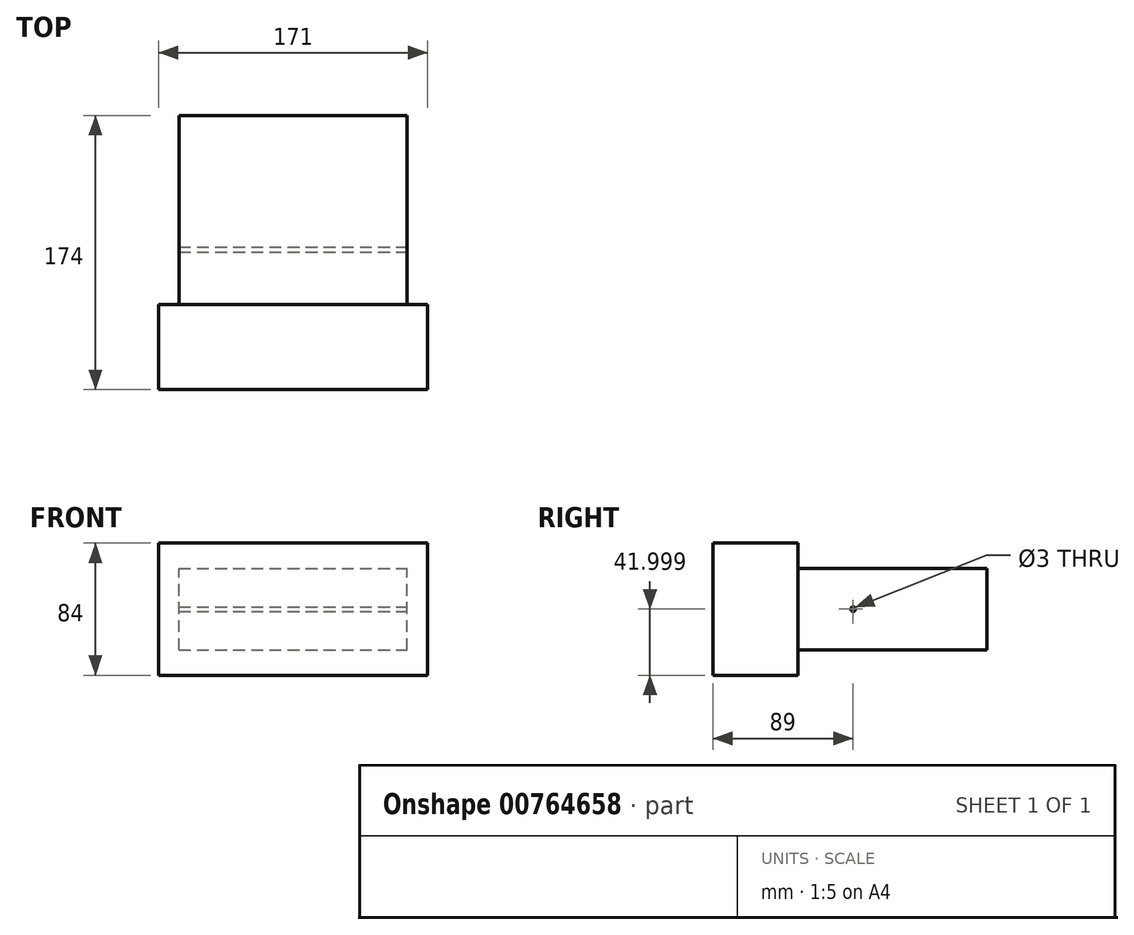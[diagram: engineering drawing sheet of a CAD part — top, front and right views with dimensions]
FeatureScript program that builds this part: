
annotation { "Feature Type Name" : "Feature", "Feature Type Description" : "" }
export const myFeature = defineFeature(function(context is Context, id is Id, definition is map)
    precondition{}
    {
        {
            var Q0;
            Q0=qCreatedBy(makeId("Front.planeOp"),FACE);
            var sketch = newSketch(context, id + "F0", { "sketchPlane" : qUnion([Q0])});
            skLineSegment(sketch, "E0.bottom", {"start": v(-55.48, -6.1) * mm, "end": v(89.52, -6.1) * mm});
            skLineSegment(sketch, "E0.top", {"start": v(-55.48, 45.9) * mm, "end": v(89.52, 45.9) * mm});
            skLineSegment(sketch, "E0.left", {"start": v(-55.48, -6.1) * mm, "end": v(-55.48, 45.9) * mm});
            skLineSegment(sketch, "E0.right", {"start": v(89.52, -6.1) * mm, "end": v(89.52, 45.9) * mm});
            skLineSegment(sketch, "E1.bottom", {"start": v(-68.48, -22.1) * mm, "end": v(102.52, -22.1) * mm});
            skLineSegment(sketch, "E1.top", {"start": v(-68.48, 61.9) * mm, "end": v(102.52, 61.9) * mm});
            skLineSegment(sketch, "E1.left", {"start": v(-68.48, -22.1) * mm, "end": v(-68.48, 61.9) * mm});
            skLineSegment(sketch, "E1.right", {"start": v(102.52, -22.1) * mm, "end": v(102.52, 61.9) * mm});
            skSolve(sketch);
        }
        {
            var Q0;
            Q0=makeQuery(id+"F0.imprint","IMPRINT",FACE,{"disambiguationData":[TD([[makeQuery(id+"F0.imprint","IMPRINT",EDGE,{"derivedFrom":sQuery(id+"F0.wireOp",EDGE,"E0.bottom")}),1.0]])]});
            extrude(context, id + "F1", {"entities" : qUnion([Q0]), "depth" : -120 * mm, "offsetDistance" : 25 * mm});
        }
        {
            var Q0;
            Q0 = qSketchRegion(id + "F0", true);
            var Q1;
            Q1=makeQuery(id+"F1.opExtrude","CAP_FACE",FACE,{"disambiguationData":[OSD([sQuery(id+"F0.wireOp",EDGE,"E0.bottom"),sQuery(id+"F0.wireOp",EDGE,"E0.top"),sQuery(id+"F0.wireOp",EDGE,"E0.left"),sQuery(id+"F0.wireOp",EDGE,"E0.right")])],"isStart":true});
            extrude(context, id + "F2", {"entities" : qUnion([Q0, Q1]), "operationType" : NewBodyOperationType.ADD, "depth" : 54 * mm, "offsetDistance" : 25 * mm});
        }
        {
            var Q0;
            Q0=qCreatedBy(makeId("Right.planeOp"),FACE);
            cPlane(context, id + "F3", {"entities" : qUnion([Q0]), "cplaneType" : CPlaneType.OFFSET, "offset" : 90 * mm, "width" : 150 * mm, "height" : 150 * mm});
        }
        {
            var Q0;
            Q0=qCreatedBy(id+"F3.planeOp",FACE);
            var sketch = newSketch(context, id + "F4", { "sketchPlane" : qUnion([Q0])});
            skPoint(sketch, "E2", {"position": v(35, 19.9) * mm});
            skSolve(sketch);
        }
        {
            var Q0;
            Q0=sQuery(id+"F4.wireOp",VERTEX,"E2");
            var Q1;
            Q1=makeQuery(id+"F1.opExtrude","SWEPT_BODY",BODY,{"disambiguationData":[OSD([sQuery(id+"F0.wireOp",EDGE,"E0.bottom"),sQuery(id+"F0.wireOp",EDGE,"E0.top"),sQuery(id+"F0.wireOp",EDGE,"E0.left"),sQuery(id+"F0.wireOp",EDGE,"E0.right")])]});
            hole(context, id + "F5", {"style" : HoleStyle.SIMPLE, "endStyle" : HoleEndStyle.THROUGH, "holeDiameter" : 3 * mm, "majorDiameter" : 5 * mm, "isTappedThrough" : true, "tappedDepth" : 12 * mm, "tapClearance" : 3, "locations" : qUnion([Q0]), "scope" : qUnion([Q1])});
        }
    });
